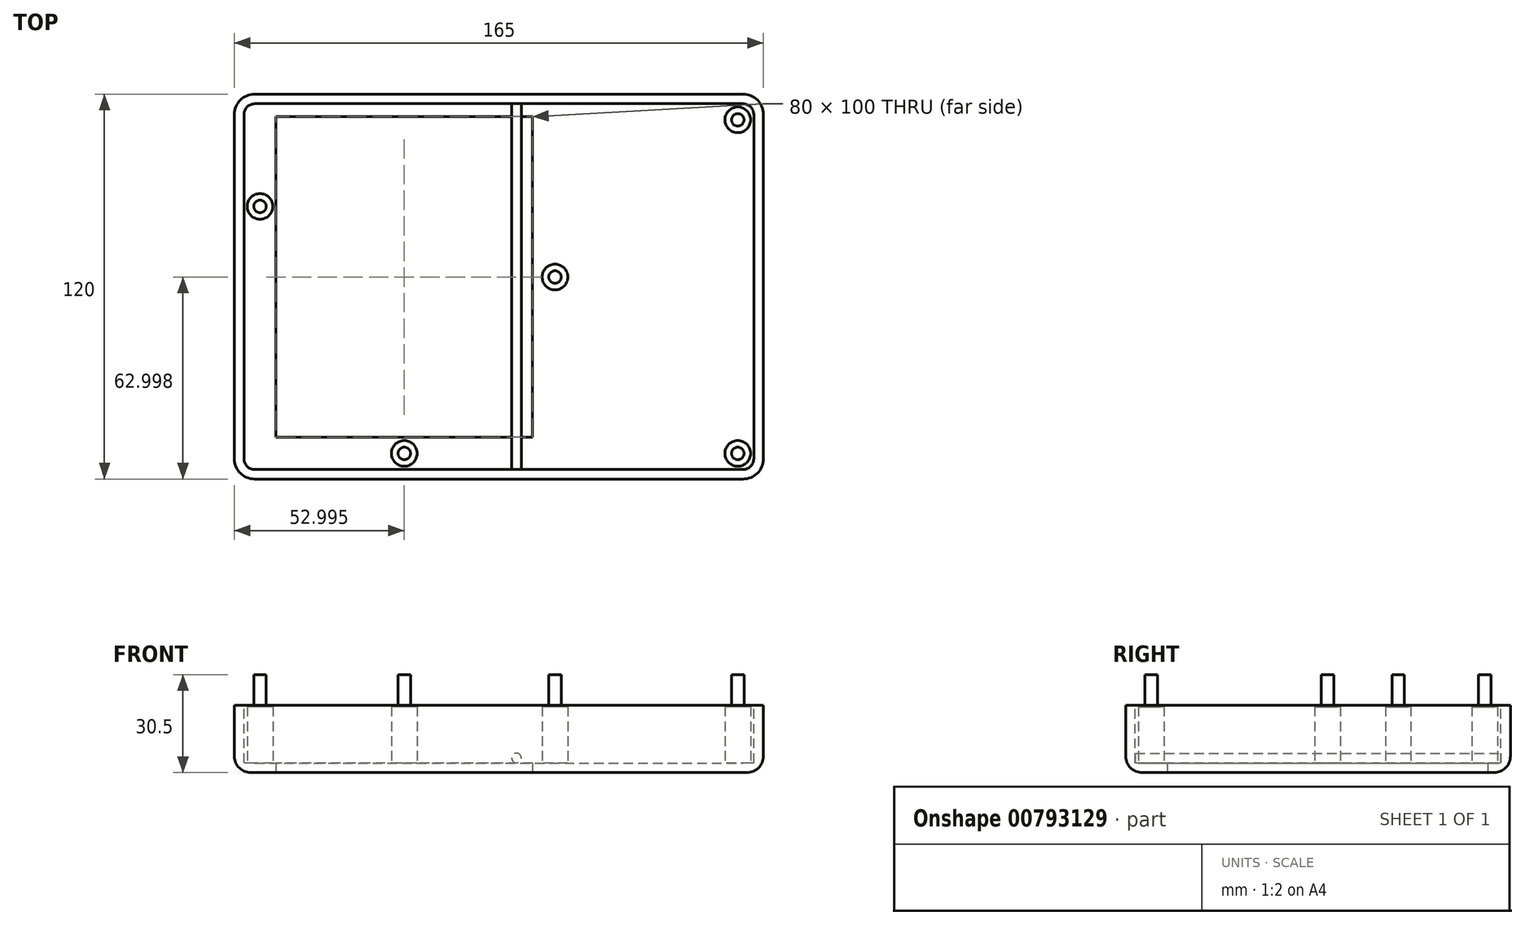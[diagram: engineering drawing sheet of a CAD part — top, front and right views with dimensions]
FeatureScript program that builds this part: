
annotation { "Feature Type Name" : "Feature", "Feature Type Description" : "" }
export const myFeature = defineFeature(function(context is Context, id is Id, definition is map)
    precondition{}
    {
        {
            var Q0;
            Q0=qCreatedBy(makeId("Top.planeOp"),FACE);
            var sketch = newSketch(context, id + "F0", { "sketchPlane" : qUnion([Q0])});
            skLineSegment(sketch, "E0.bottom", {"start": v(-76.98, -45.25) * mm, "end": v(75.32, -45.25) * mm});
            skLineSegment(sketch, "E0.top", {"start": v(-76.98, 74.75) * mm, "end": v(75.32, 74.75) * mm});
            skLineSegment(sketch, "E0.left", {"start": v(-83.33, -38.9) * mm, "end": v(-83.33, 68.4) * mm});
            skLineSegment(sketch, "E0.right", {"start": v(81.67, -38.9) * mm, "end": v(81.67, 68.4) * mm});
            skPoint(sketch, "E1.visualSharp", {"position": v(-83.33, 74.75) * mm});
            skArc(sketch, "E1.filletArc", {"start": v(-76.98, 74.75) * mm, "mid": v(-81.47, 72.89) * mm, "end": v(-83.33, 68.4) * mm});
            skPoint(sketch, "E2.visualSharp", {"position": v(81.67, 74.75) * mm});
            skArc(sketch, "E2.filletArc", {"start": v(81.67, 68.4) * mm, "mid": v(79.8, 72.89) * mm, "end": v(75.32, 74.75) * mm});
            skPoint(sketch, "E3.visualSharp", {"position": v(81.67, -45.25) * mm});
            skArc(sketch, "E3.filletArc", {"start": v(75.32, -45.25) * mm, "mid": v(79.8, -43.4) * mm, "end": v(81.67, -38.9) * mm});
            skPoint(sketch, "E4.visualSharp", {"position": v(-83.33, -45.25) * mm});
            skArc(sketch, "E4.filletArc", {"start": v(-83.33, -38.9) * mm, "mid": v(-81.47, -43.4) * mm, "end": v(-76.98, -45.25) * mm});
            skSolve(sketch);
        }
        {
            var Q0;
            Q0=qSketchRegion(id+"F0",true);
            extrude(context, id + "F1", {"entities" : qUnion([Q0]), "depth" : 21 * mm, "offsetDistance" : 25.4 * mm});
        }
        {
            var Q0;
            Q0=makeQuery(id+"F1.opExtrude","CAP_FACE",FACE,{"disambiguationData":[OSD([sQuery(id+"F0.wireOp",EDGE,"E0.bottom"),sQuery(id+"F0.wireOp",EDGE,"E0.top"),sQuery(id+"F0.wireOp",EDGE,"E0.left"),sQuery(id+"F0.wireOp",EDGE,"E0.right")])],"isStart":false});
            shell(context, id + "F2", {"entities" : qUnion([Q0]), "thickness" : 3 * mm});
        }
        {
            var Q0;
            Q0=makeQuery(id+"F1.opExtrude","CAP_EDGE",EDGE,{"disambiguationData":[OSD([sQuery(id+"F0.wireOp",EDGE,"E1.filletArc")])],"isStart":true});
            fillet(context, id + "F3", {"entities" : qUnion([Q0]), "radius" : 5.08 * mm, "tangentPropagation" : true, "allowEdgeOverflow" : false});
        }
        {
            var Q0;
            Q0=makeQuery(id+"F2.opShell","OFFSET_FACE",FACE,{"disambiguationData":[OSD([sQuery(id+"F0.wireOp",EDGE,"E0.bottom"),sQuery(id+"F0.wireOp",EDGE,"E0.top"),sQuery(id+"F0.wireOp",EDGE,"E0.left"),sQuery(id+"F0.wireOp",EDGE,"E0.right"),sQuery(id+"F0.wireOp",EDGE,"E1.filletArc"),sQuery(id+"F0.wireOp",EDGE,"E2.filletArc"),sQuery(id+"F0.wireOp",EDGE,"E3.filletArc"),sQuery(id+"F0.wireOp",EDGE,"E4.filletArc")])]});
            var sketch = newSketch(context, id + "F4", { "sketchPlane" : qUnion([Q0])});
            skCircle(sketch, "E5", {"center": v(73.67, -37.25) * mm, "radius": 4 * mm});
            skCircle(sketch, "E6", {"center": v(73.67, 66.75) * mm, "radius": 4 * mm});
            skCircle(sketch, "E7", {"center": v(16.67, 17.75) * mm, "radius": 4 * mm});
            skCircle(sketch, "E8", {"center": v(-75.33, 39.75) * mm, "radius": 4 * mm});
            skCircle(sketch, "E9", {"center": v(-30.33, -37.25) * mm, "radius": 4 * mm});
            skSolve(sketch);
        }
        {
            var Q0;
            Q0=qSketchRegion(id+"F4",true);
            extrude(context, id + "F5", {"entities" : qUnion([Q0]), "operationType" : NewBodyOperationType.ADD, "depth" : 17.5 * mm, "offsetDistance" : 25 * mm});
        }
        {
            var Q0;
            Q0=makeQuery(id+"F5.opExtrude","CAP_FACE",FACE,{"disambiguationData":[OSD([sQuery(id+"F4.wireOp",EDGE,"E5")])],"isStart":false});
            var sketch = newSketch(context, id + "F6", { "sketchPlane" : qUnion([Q0])});
            skCircle(sketch, "E10", {"center": v(73.67, -37.25) * mm, "radius": 1.95 * mm});
            skCircle(sketch, "E11", {"center": v(16.67, 17.75) * mm, "radius": 1.95 * mm});
            skCircle(sketch, "E12", {"center": v(73.67, 66.75) * mm, "radius": 1.95 * mm});
            skCircle(sketch, "E13", {"center": v(-30.33, -37.25) * mm, "radius": 1.95 * mm});
            skCircle(sketch, "E14", {"center": v(-75.33, 39.75) * mm, "radius": 1.95 * mm});
            skSolve(sketch);
        }
        {
            var Q0;
            Q0=qSketchRegion(id+"F6",true);
            extrude(context, id + "F7", {"entities" : qUnion([Q0]), "operationType" : NewBodyOperationType.ADD, "depth" : 10 * mm, "offsetDistance" : 25 * mm});
        }
        {
            var Q0;
            Q0=makeQuery(id+"F1.opExtrude","CAP_FACE",FACE,{"disambiguationData":[OSD([sQuery(id+"F0.wireOp",EDGE,"E0.bottom"),sQuery(id+"F0.wireOp",EDGE,"E0.top"),sQuery(id+"F0.wireOp",EDGE,"E0.left"),sQuery(id+"F0.wireOp",EDGE,"E0.right"),sQuery(id+"F0.wireOp",EDGE,"E1.filletArc"),sQuery(id+"F0.wireOp",EDGE,"E2.filletArc"),sQuery(id+"F0.wireOp",EDGE,"E3.filletArc"),sQuery(id+"F0.wireOp",EDGE,"E4.filletArc")])],"isStart":true});
            var sketch = newSketch(context, id + "F8", { "sketchPlane" : qUnion([Q0])});
            skLineSegment(sketch, "E15.bottom", {"start": v(-70.33, -67.75) * mm, "end": v(9.67, -67.75) * mm});
            skLineSegment(sketch, "E15.top", {"start": v(-70.33, 32.25) * mm, "end": v(9.67, 32.25) * mm});
            skLineSegment(sketch, "E15.left", {"start": v(-70.33, -67.75) * mm, "end": v(-70.33, 32.25) * mm});
            skLineSegment(sketch, "E15.right", {"start": v(9.67, -67.75) * mm, "end": v(9.67, 32.25) * mm});
            skSolve(sketch);
        }
        {
            var Q0;
            Q0 = qSketchRegion(id + "F8", true);
            extrude(context, id + "F9", {"entities" : qUnion([Q0]), "operationType" : NewBodyOperationType.REMOVE, "oppositeDirection" : true, "depth" : 25 * mm, "offsetDistance" : 25 * mm});
        }
        {
            var Q0;
            Q0=makeQuery(id+"F2.opShell","OFFSET_FACE",FACE,{"disambiguationData":[OSD([sQuery(id+"F0.wireOp",EDGE,"E0.top")])]});
            var sketch = newSketch(context, id + "F10", { "sketchPlane" : qUnion([Q0])});
            skCircle(sketch, "E16", {"center": v(4.67, 4.55) * mm, "radius": 1.5 * mm});
            skSolve(sketch);
        }
        {
            var Q0;
            Q0 = qSketchRegion(id + "F10", true);
            extrude(context, id + "F11", {"entities" : qUnion([Q0]), "operationType" : NewBodyOperationType.ADD, "depth" : 115 * mm, "offsetDistance" : 25 * mm});
        }
    });
